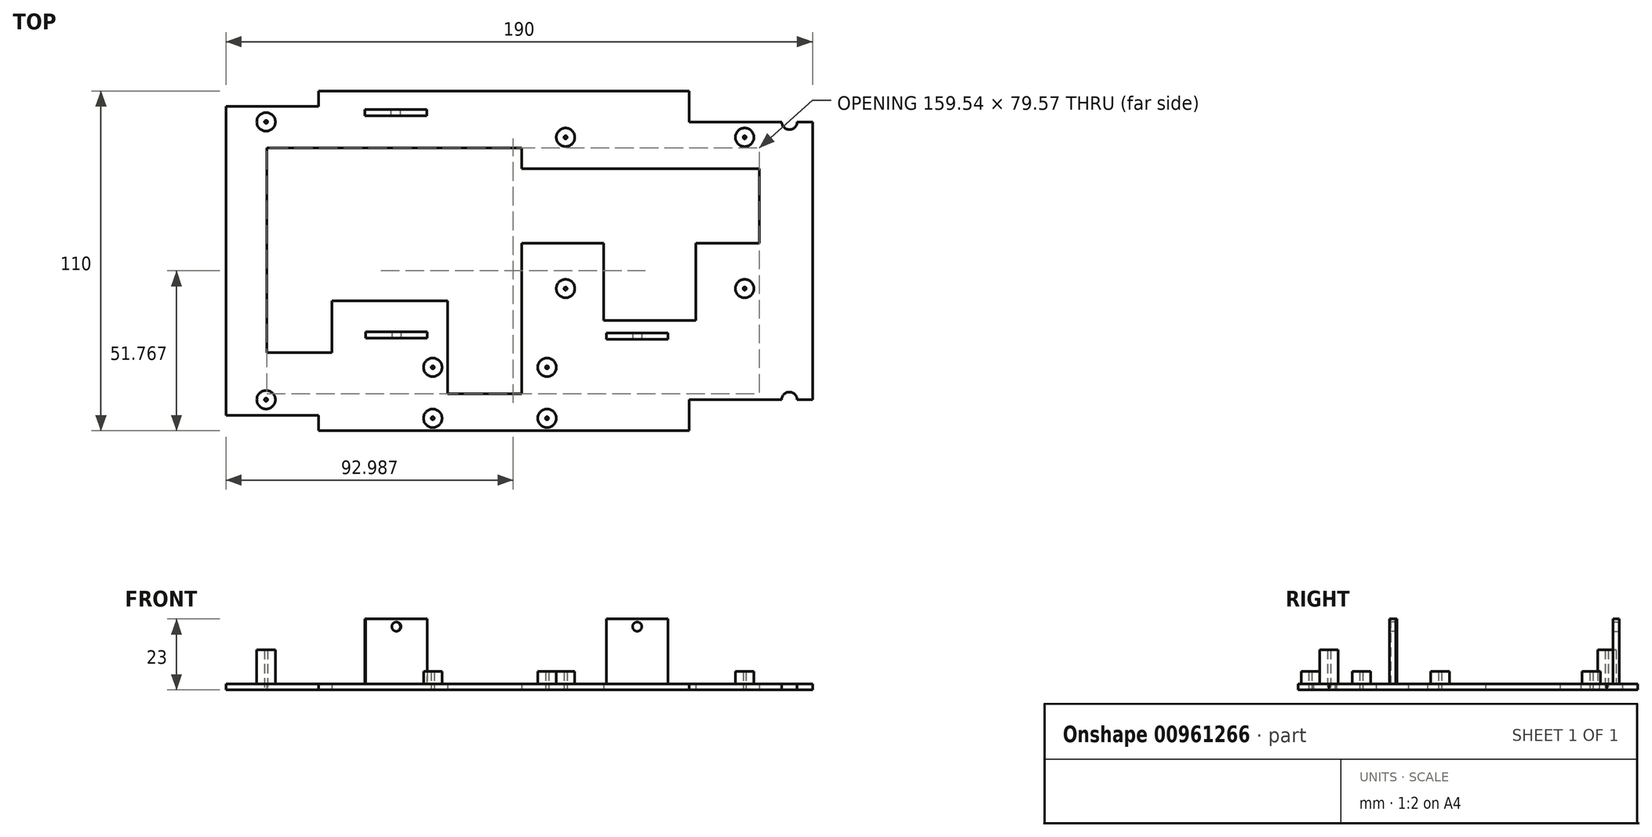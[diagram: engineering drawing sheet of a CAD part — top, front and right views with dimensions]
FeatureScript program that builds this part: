
annotation { "Feature Type Name" : "Feature", "Feature Type Description" : "" }
export const myFeature = defineFeature(function(context is Context, id is Id, definition is map)
    precondition{}
    {
        {
            var Q0;
            Q0=qCreatedBy(makeId("Top.planeOp"),FACE);
            var sketch = newSketch(context, id + "F0", { "sketchPlane" : qUnion([Q0])});
            skLineSegment(sketch, "E0.bottom", {"start": v(-140.86, 43.78) * mm, "end": v(-20.86, 43.78) * mm});
            skLineSegment(sketch, "E0.top", {"start": v(-140.86, -66.22) * mm, "end": v(-20.86, -66.22) * mm});
            skLineSegment(sketch, "E0.left", {"start": v(-170.86, 38.78) * mm, "end": v(-170.86, -61.22) * mm});
            skLineSegment(sketch, "E0.right", {"start": v(19.14, 33.78) * mm, "end": v(19.14, -56.22) * mm});
            skCircle(sketch, "E1", {"center": v(-157.86, 33.78) * mm, "radius": 3 * mm});
            skCircle(sketch, "E2", {"center": v(-157.86, -56.22) * mm, "radius": 3 * mm});
            skLineSegment(sketch, "E3.bottom", {"start": v(-125.86, 37.78) * mm, "end": v(-105.86, 37.78) * mm});
            skLineSegment(sketch, "E3.top", {"start": v(-125.86, 35.78) * mm, "end": v(-105.86, 35.78) * mm});
            skLineSegment(sketch, "E3.left", {"start": v(-125.86, 37.78) * mm, "end": v(-125.86, 35.78) * mm});
            skLineSegment(sketch, "E3.right", {"start": v(-105.86, 37.78) * mm, "end": v(-105.86, 35.78) * mm});
            skLineSegment(sketch, "E4.bottom", {"start": v(-125.65, -34.22) * mm, "end": v(-105.65, -34.22) * mm});
            skLineSegment(sketch, "E4.top", {"start": v(-125.65, -36.22) * mm, "end": v(-105.65, -36.22) * mm});
            skLineSegment(sketch, "E4.left", {"start": v(-125.65, -34.22) * mm, "end": v(-125.65, -36.22) * mm});
            skLineSegment(sketch, "E4.right", {"start": v(-105.65, -34.22) * mm, "end": v(-105.65, -36.22) * mm});
            skCircle(sketch, "E5", {"center": v(-103.86, -62.22) * mm, "radius": 3 * mm});
            skCircle(sketch, "E6", {"center": v(-103.86, -45.72) * mm, "radius": 3 * mm});
            skCircle(sketch, "E7", {"center": v(-66.86, -62.22) * mm, "radius": 3 * mm});
            skCircle(sketch, "E8", {"center": v(-66.86, -45.72) * mm, "radius": 3 * mm});
            skCircle(sketch, "E9", {"center": v(-2.86, 28.78) * mm, "radius": 3 * mm});
            skCircle(sketch, "E10", {"center": v(-60.86, 28.78) * mm, "radius": 3 * mm});
            skCircle(sketch, "E11", {"center": v(-60.86, -20.22) * mm, "radius": 3 * mm});
            skCircle(sketch, "E12", {"center": v(-2.86, -20.22) * mm, "radius": 3 * mm});
            skLineSegment(sketch, "E13.bottom", {"start": v(-157.64, 25.33) * mm, "end": v(-75.02, 25.33) * mm});
            skLineSegment(sketch, "E13.top", {"start": v(-136.5, -24.24) * mm, "end": v(-99.02, -24.24) * mm});
            skLineSegment(sketch, "E13.left", {"start": v(-157.64, 25.33) * mm, "end": v(-157.64, -24.24) * mm});
            skLineSegment(sketch, "E13.right", {"start": v(-75.02, 25.33) * mm, "end": v(-75.02, 18.62) * mm});
            skLineSegment(sketch, "E14.top", {"start": v(-157.64, -40.9) * mm, "end": v(-136.5, -40.9) * mm});
            skLineSegment(sketch, "E14.left", {"start": v(-157.64, -24.24) * mm, "end": v(-157.64, -40.9) * mm});
            skLineSegment(sketch, "E14.right", {"start": v(-136.5, -24.24) * mm, "end": v(-136.5, -40.9) * mm});
            skLineSegment(sketch, "E15.bottom", {"start": v(-75.02, 18.62) * mm, "end": v(1.9, 18.62) * mm});
            skLineSegment(sketch, "E15.top", {"start": v(-75.02, -5.52) * mm, "end": v(-48.53, -5.52) * mm});
            skLineSegment(sketch, "E15.right", {"start": v(1.9, 18.62) * mm, "end": v(1.9, -5.52) * mm});
            skLineSegment(sketch, "E16.top", {"start": v(-48.53, -30.52) * mm, "end": v(-18.61, -30.52) * mm});
            skLineSegment(sketch, "E16.left", {"start": v(-48.53, -5.52) * mm, "end": v(-48.53, -30.52) * mm});
            skLineSegment(sketch, "E16.right", {"start": v(-18.61, -5.52) * mm, "end": v(-18.61, -30.52) * mm});
            skCircle(sketch, "E17", {"center": v(-157.86, 33.78) * mm, "radius": 0.5 * mm});
            skCircle(sketch, "E18", {"center": v(-157.86, -56.22) * mm, "radius": 0.5 * mm});
            skCircle(sketch, "E19", {"center": v(-103.86, -45.72) * mm, "radius": 0.5 * mm});
            skCircle(sketch, "E20", {"center": v(-103.86, -62.22) * mm, "radius": 0.5 * mm});
            skCircle(sketch, "E21", {"center": v(-66.86, -45.72) * mm, "radius": 0.5 * mm});
            skCircle(sketch, "E22", {"center": v(-66.86, -62.22) * mm, "radius": 0.5 * mm});
            skCircle(sketch, "E23", {"center": v(-60.86, -20.22) * mm, "radius": 0.5 * mm});
            skCircle(sketch, "E24", {"center": v(-2.86, -20.22) * mm, "radius": 0.5 * mm});
            skCircle(sketch, "E25", {"center": v(-2.86, 28.78) * mm, "radius": 0.5 * mm});
            skCircle(sketch, "E26", {"center": v(-60.86, 28.78) * mm, "radius": 0.5 * mm});
            skLineSegment(sketch, "E27.trimOffspring", {"start": v(-75.02, -5.52) * mm, "end": v(-75.02, -24.24) * mm});
            skLineSegment(sketch, "E28.trimOffspring", {"start": v(-18.61, -5.52) * mm, "end": v(1.9, -5.52) * mm});
            skLineSegment(sketch, "E29", {"start": v(-170.86, 38.78) * mm, "end": v(-140.86, 38.78) * mm});
            skLineSegment(sketch, "E30", {"start": v(-140.86, 38.78) * mm, "end": v(-140.86, 43.78) * mm});
            skLineSegment(sketch, "E31", {"start": v(-170.86, -61.22) * mm, "end": v(-140.86, -61.22) * mm});
            skLineSegment(sketch, "E32", {"start": v(-140.86, -61.22) * mm, "end": v(-140.86, -66.22) * mm});
            skLineSegment(sketch, "E33", {"start": v(19.14, 33.78) * mm, "end": v(14.14, 33.78) * mm});
            skLineSegment(sketch, "E34", {"start": v(-20.86, 33.78) * mm, "end": v(-20.86, 43.78) * mm});
            skLineSegment(sketch, "E35", {"start": v(19.14, -56.22) * mm, "end": v(14.14, -56.22) * mm});
            skLineSegment(sketch, "E36", {"start": v(-20.86, -56.22) * mm, "end": v(-20.86, -66.22) * mm});
            skLineSegment(sketch, "E37.bottom", {"start": v(-47.65, -34.64) * mm, "end": v(-27.65, -34.64) * mm});
            skLineSegment(sketch, "E37.top", {"start": v(-47.65, -36.64) * mm, "end": v(-27.65, -36.64) * mm});
            skLineSegment(sketch, "E37.left", {"start": v(-47.65, -34.64) * mm, "end": v(-47.65, -36.64) * mm});
            skLineSegment(sketch, "E37.right", {"start": v(-27.65, -34.64) * mm, "end": v(-27.65, -36.64) * mm});
            skLineSegment(sketch, "E38", {"start": v(-75.02, -24.24) * mm, "end": v(-75.02, -54.24) * mm});
            skLineSegment(sketch, "E39", {"start": v(-75.02, -54.24) * mm, "end": v(-99.02, -54.24) * mm});
            skLineSegment(sketch, "E40", {"start": v(-99.02, -54.24) * mm, "end": v(-99.02, -24.24) * mm});
            skArc(sketch, "E41", {"start": v(14.14, -56.22) * mm, "mid": v(11.64, -53.72) * mm, "end": v(9.14, -56.22) * mm});
            skLineSegment(sketch, "E42.trimOffspring", {"start": v(9.14, -56.22) * mm, "end": v(-20.86, -56.22) * mm});
            skArc(sketch, "E43", {"start": v(9.14, 33.78) * mm, "mid": v(11.64, 31.28) * mm, "end": v(14.14, 33.78) * mm});
            skLineSegment(sketch, "E44.trimOffspring", {"start": v(9.14, 33.78) * mm, "end": v(-20.86, 33.78) * mm});
            skSolve(sketch);
        }
        {
            var Q0;
            Q0=makeQuery(id+"F0.imprint","IMPRINT",FACE,{"disambiguationData":[TD([[makeQuery(id+"F0.imprint","IMPRINT",EDGE,{"derivedFrom":sQuery(id+"F0.wireOp",EDGE,"E0.bottom")}),-1.0]])]});
            extrude(context, id + "F1", {"entities" : qUnion([Q0]), "depth" : 2 * mm, "offsetDistance" : 25 * mm});
        }
        {
            var Q0;
            Q0=makeQuery(id+"F0.imprint","IMPRINT",FACE,{"disambiguationData":[TD([[makeQuery(id+"F0.imprint","IMPRINT",EDGE,{"derivedFrom":sQuery(id+"F0.wireOp",EDGE,"E1")}),1.0]])]});
            var Q1;
            Q1=makeQuery(id+"F0.imprint","IMPRINT",FACE,{"disambiguationData":[TD([[makeQuery(id+"F0.imprint","IMPRINT",EDGE,{"derivedFrom":sQuery(id+"F0.wireOp",EDGE,"E2")}),1.0]])]});
            extrude(context, id + "F2", {"entities" : qUnion([Q0, Q1]), "operationType" : NewBodyOperationType.ADD, "depth" : 13 * mm, "offsetDistance" : 25 * mm});
        }
        {
            var Q0;
            Q0=makeQuery(id+"F0.imprint","IMPRINT",FACE,{"disambiguationData":[TD([[makeQuery(id+"F0.imprint","IMPRINT",EDGE,{"derivedFrom":sQuery(id+"F0.wireOp",EDGE,"E4.bottom")}),-1.0]])]});
            var Q1;
            Q1=makeQuery(id+"F0.imprint","IMPRINT",FACE,{"disambiguationData":[TD([[makeQuery(id+"F0.imprint","IMPRINT",EDGE,{"derivedFrom":sQuery(id+"F0.wireOp",EDGE,"E3.bottom")}),-1.0]])]});
            var Q2;
            Q2=makeQuery(id+"F0.imprint","IMPRINT",FACE,{"disambiguationData":[TD([[makeQuery(id+"F0.imprint","IMPRINT",EDGE,{"derivedFrom":sQuery(id+"F0.wireOp",EDGE,"E37.bottom")}),-1.0]])]});
            extrude(context, id + "F3", {"entities" : qUnion([Q0, Q1, Q2]), "operationType" : NewBodyOperationType.ADD, "depth" : 23 * mm, "offsetDistance" : 25 * mm});
        }
        {
            var Q0;
            Q0=makeQuery(id+"F0.imprint","IMPRINT",FACE,{"disambiguationData":[TD([[makeQuery(id+"F0.imprint","IMPRINT",EDGE,{"derivedFrom":sQuery(id+"F0.wireOp",EDGE,"E10")}),1.0]])]});
            var Q1;
            Q1=makeQuery(id+"F0.imprint","IMPRINT",FACE,{"disambiguationData":[TD([[makeQuery(id+"F0.imprint","IMPRINT",EDGE,{"derivedFrom":sQuery(id+"F0.wireOp",EDGE,"E9")}),1.0]])]});
            var Q2;
            Q2=makeQuery(id+"F0.imprint","IMPRINT",FACE,{"disambiguationData":[TD([[makeQuery(id+"F0.imprint","IMPRINT",EDGE,{"derivedFrom":sQuery(id+"F0.wireOp",EDGE,"E12")}),1.0]])]});
            var Q3;
            Q3=makeQuery(id+"F0.imprint","IMPRINT",FACE,{"disambiguationData":[TD([[makeQuery(id+"F0.imprint","IMPRINT",EDGE,{"derivedFrom":sQuery(id+"F0.wireOp",EDGE,"E11")}),1.0]])]});
            var Q4;
            Q4=makeQuery(id+"F0.imprint","IMPRINT",FACE,{"disambiguationData":[TD([[makeQuery(id+"F0.imprint","IMPRINT",EDGE,{"derivedFrom":sQuery(id+"F0.wireOp",EDGE,"E8")}),1.0]])]});
            var Q5;
            Q5=makeQuery(id+"F0.imprint","IMPRINT",FACE,{"disambiguationData":[TD([[makeQuery(id+"F0.imprint","IMPRINT",EDGE,{"derivedFrom":sQuery(id+"F0.wireOp",EDGE,"E7")}),1.0]])]});
            var Q6;
            Q6=makeQuery(id+"F0.imprint","IMPRINT",FACE,{"disambiguationData":[TD([[makeQuery(id+"F0.imprint","IMPRINT",EDGE,{"derivedFrom":sQuery(id+"F0.wireOp",EDGE,"E5")}),1.0]])]});
            var Q7;
            Q7=makeQuery(id+"F0.imprint","IMPRINT",FACE,{"disambiguationData":[TD([[makeQuery(id+"F0.imprint","IMPRINT",EDGE,{"derivedFrom":sQuery(id+"F0.wireOp",EDGE,"E6")}),1.0]])]});
            extrude(context, id + "F4", {"entities" : qUnion([Q0, Q1, Q2, Q3, Q4, Q5, Q6, Q7]), "operationType" : NewBodyOperationType.ADD, "depth" : 6 * mm, "offsetDistance" : 25 * mm});
        }
        {
            var Q0;
            Q0=makeQuery(id+"F3.opExtrude","SWEPT_FACE",FACE,{"disambiguationData":[OSD([sQuery(id+"F0.wireOp",EDGE,"E4.top")])]});
            var sketch = newSketch(context, id + "F5", { "sketchPlane" : qUnion([Q0])});
            skCircle(sketch, "E45", {"center": v(-115.65, 20.5) * mm, "radius": 1.5 * mm});
            skPoint(sketch, "E45.centerSnap0", {"position": v(-115.65, 23) * mm});
            skSolve(sketch);
        }
        {
            var Q0;
            Q0 = qSketchRegion(id + "F5", true);
            extrude(context, id + "F6", {"entities" : qUnion([Q0]), "operationType" : NewBodyOperationType.REMOVE, "oppositeDirection" : true, "depth" : 25 * mm, "offsetDistance" : 25 * mm});
        }
        {
            var Q0;
            Q0=makeQuery(id+"F3.opExtrude","SWEPT_FACE",FACE,{"disambiguationData":[OSD([sQuery(id+"F0.wireOp",EDGE,"E3.bottom")])]});
            var sketch = newSketch(context, id + "F7", { "sketchPlane" : qUnion([Q0])});
            skCircle(sketch, "E46", {"center": v(115.86, 20.5) * mm, "radius": 1.5 * mm});
            skPoint(sketch, "E46.centerSnap0", {"position": v(115.86, 23) * mm});
            skSolve(sketch);
        }
        {
            var Q0;
            Q0=makeQuery(id+"F7.imprint","IMPRINT",FACE,{"disambiguationData":[TD([[makeQuery(id+"F7.imprint","IMPRINT",EDGE,{"derivedFrom":sQuery(id+"F7.wireOp",EDGE,"E46")}),1.0]])]});
            extrude(context, id + "F8", {"entities" : qUnion([Q0]), "operationType" : NewBodyOperationType.REMOVE, "oppositeDirection" : true, "depth" : 5 * mm, "offsetDistance" : 25 * mm});
        }
        {
            var Q0;
            Q0=makeQuery(id+"F3.opExtrude","SWEPT_FACE",FACE,{"disambiguationData":[OSD([sQuery(id+"F0.wireOp",EDGE,"E37.top")])]});
            var sketch = newSketch(context, id + "F9", { "sketchPlane" : qUnion([Q0])});
            skCircle(sketch, "E47", {"center": v(-37.65, 20.5) * mm, "radius": 1.5 * mm});
            skPoint(sketch, "E47.centerSnap0", {"position": v(-37.65, 23) * mm});
            skSolve(sketch);
        }
        {
            var Q0;
            Q0=makeQuery(id+"F9.imprint","IMPRINT",FACE,{"disambiguationData":[TD([[makeQuery(id+"F9.imprint","IMPRINT",EDGE,{"derivedFrom":sQuery(id+"F9.wireOp",EDGE,"E47")}),1.0]])]});
            extrude(context, id + "F10", {"entities" : qUnion([Q0]), "operationType" : NewBodyOperationType.REMOVE, "oppositeDirection" : true, "depth" : 5 * mm, "offsetDistance" : 25 * mm});
        }
    });
